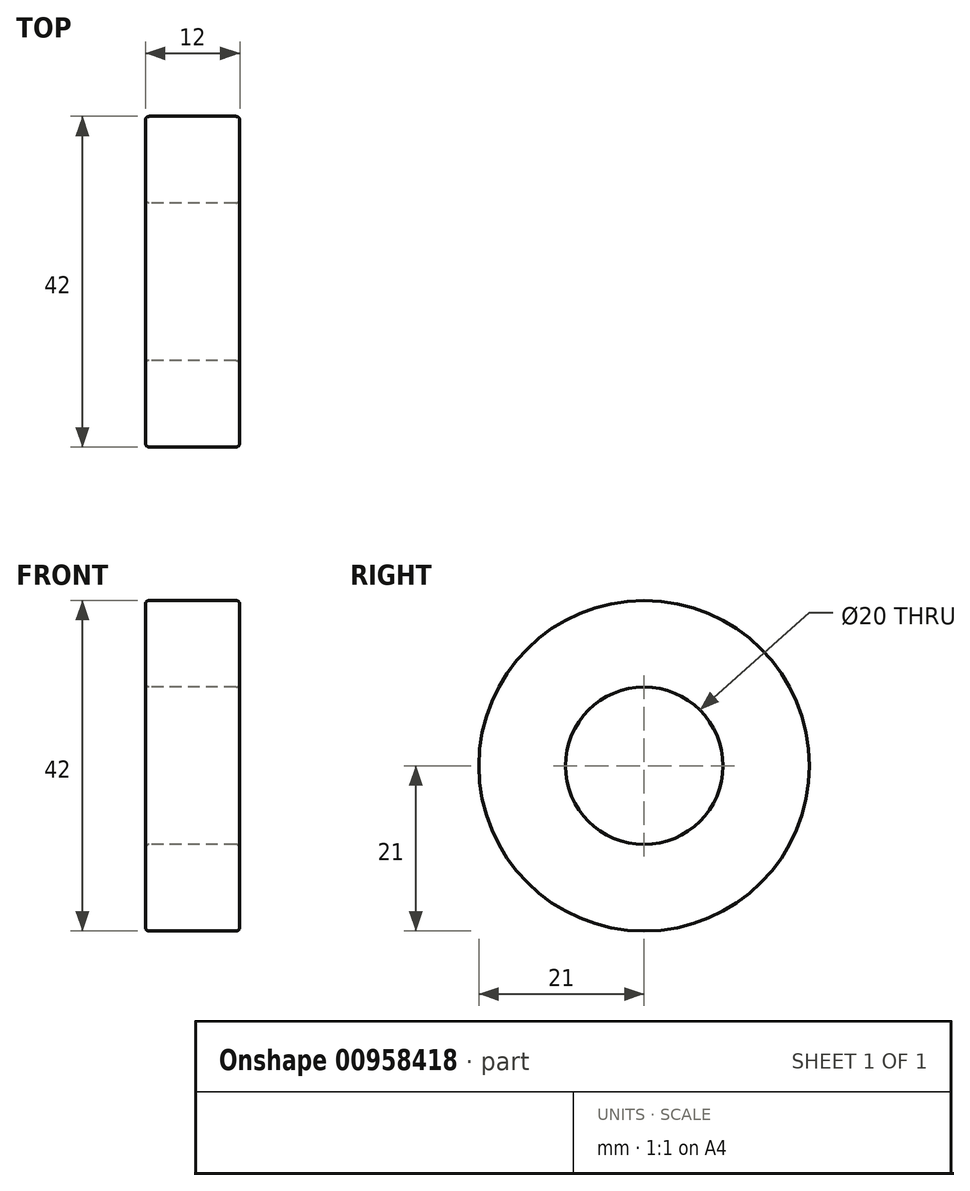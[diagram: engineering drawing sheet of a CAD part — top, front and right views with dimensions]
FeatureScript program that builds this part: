
annotation { "Feature Type Name" : "Feature", "Feature Type Description" : "" }
export const myFeature = defineFeature(function(context is Context, id is Id, definition is map)
    precondition{}
    {
        {
            var Q0;
            Q0=qCreatedBy(makeId("Front.planeOp"),FACE);
            var sketch = newSketch(context, id + "F0", { "sketchPlane" : qUnion([Q0])});
            skLineSegment(sketch, "E0.bottom", {"start": v(12.27, 21) * mm, "end": v(0.27, 21) * mm});
            skLineSegment(sketch, "E0.top", {"start": v(12.27, 10) * mm, "end": v(0.27, 10) * mm});
            skLineSegment(sketch, "E0.left", {"start": v(12.27, 21) * mm, "end": v(12.27, 10) * mm});
            skLineSegment(sketch, "E0.right", {"start": v(0.27, 21) * mm, "end": v(0.27, 10) * mm});
            skLineSegment(sketch, "E1", {"start": v(0, 0) * mm, "end": v(5.54, 0) * mm});
            skSolve(sketch);
        }
        {
            var Q0;
            Q0=qSketchRegion(id+"F0",true);
            var Q1;
            Q1=sQuery(id+"F0.wireOp",EDGE,"E1");
            revolve(context, id + "F1", {"surfaceOperationType" : NewSurfaceOperationType.NEW, "entities" : qUnion([Q0]), "axis" : qUnion([Q1]), "revolveType" : RevolveType.FULL});
        }
        {
            var Q0;
            Q0=makeQuery(id+"F1.opRevolve","SWEPT_FACE",FACE,{"disambiguationData":[OSD([sQuery(id+"F0.wireOp",EDGE,"E0.bottom")])]});
            var Q1;
            Q1=makeQuery(id+"F1.opRevolve","SWEPT_FACE",FACE,{"disambiguationData":[OSD([sQuery(id+"F0.wireOp",EDGE,"E0.top")])]});
            fillet(context, id + "F2", {"entities" : qUnion([Q0, Q1]), "radius" : 0.5 * mm, "tangentPropagation" : true, "allowEdgeOverflow" : false});
        }
    });
